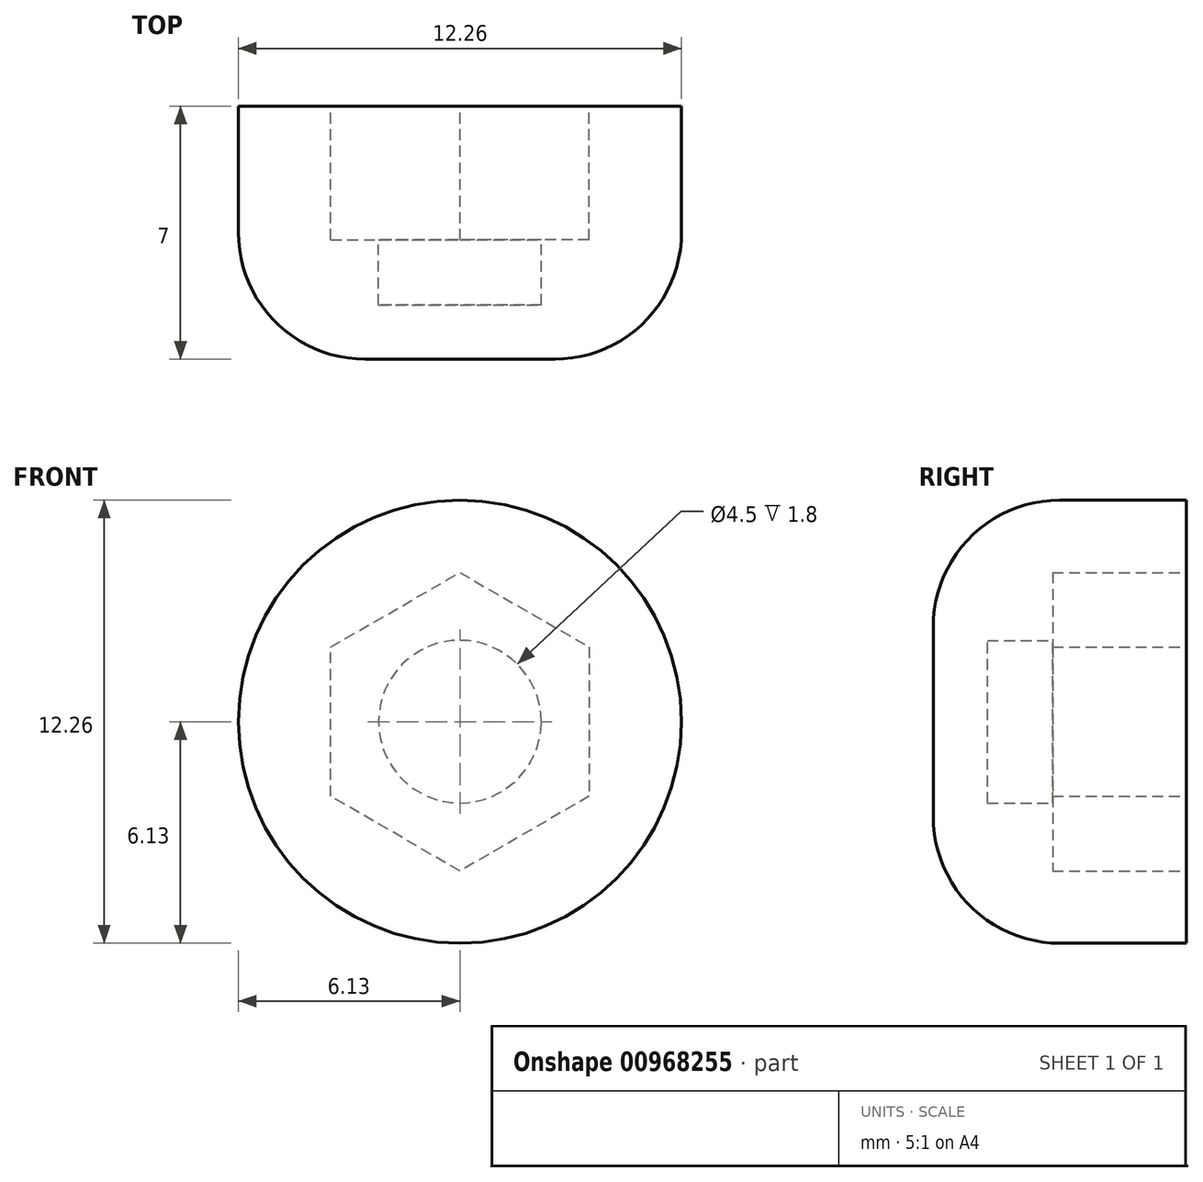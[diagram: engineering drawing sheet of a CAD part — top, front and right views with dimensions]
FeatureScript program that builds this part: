
annotation { "Feature Type Name" : "Feature", "Feature Type Description" : "" }
export const myFeature = defineFeature(function(context is Context, id is Id, definition is map)
    precondition{}
    {
        {
            var Q0;
            Q0=qCreatedBy(makeId("Front.planeOp"),FACE);
            var sketch = newSketch(context, id + "F0", { "sketchPlane" : qUnion([Q0])});
            skCircle(sketch, "E0", {"center": v(0, 0) * mm, "radius": 6.13 * mm});
            skCircle(sketch, "E1.cCircle", {"center": v(0, 0) * mm, "radius": 3.58 * mm, "construction": true});
            skLineSegment(sketch, "E1.0", {"start": v(3.57, -2.06) * mm, "end": v(0, -4.13) * mm});
            skLineSegment(sketch, "E1.1", {"start": v(0, -4.13) * mm, "end": v(-3.58, -2.06) * mm});
            skLineSegment(sketch, "E1.2", {"start": v(-3.58, -2.06) * mm, "end": v(-3.57, 2.06) * mm});
            skLineSegment(sketch, "E1.3", {"start": v(-3.58, 2.06) * mm, "end": v(0, 4.13) * mm});
            skLineSegment(sketch, "E1.4", {"start": v(0, 4.13) * mm, "end": v(3.57, 2.06) * mm});
            skLineSegment(sketch, "E1.5", {"start": v(3.58, 2.06) * mm, "end": v(3.57, -2.06) * mm});
            skPoint(sketch, "E1.0.midPoint", {"position": v(1.79, -3.1) * mm});
            skCircle(sketch, "E2", {"center": v(0, 0) * mm, "radius": 2.25 * mm});
            skSolve(sketch);
        }
        {
            var Q0;
            Q0=makeQuery(id+"F0.imprint","IMPRINT",FACE,{"disambiguationData":[TD([[makeQuery(id+"F0.imprint","IMPRINT",EDGE,{"derivedFrom":sQuery(id+"F0.wireOp",EDGE,"E0")}),1.0]])]});
            var Q1;
            Q1=makeQuery(id+"F0.imprint","IMPRINT",FACE,{"disambiguationData":[TD([[makeQuery(id+"F0.imprint","IMPRINT",EDGE,{"derivedFrom":sQuery(id+"F0.wireOp",EDGE,"E1.0")}),-1.0]])]});
            var Q2;
            Q2=makeQuery(id+"F0.imprint","IMPRINT",FACE,{"disambiguationData":[TD([[makeQuery(id+"F0.imprint","IMPRINT",EDGE,{"derivedFrom":sQuery(id+"F0.wireOp",EDGE,"E2")}),1.0]])]});
            extrude(context, id + "F1", {"entities" : qUnion([Q0, Q1, Q2]), "depth" : 7 * mm, "offsetDistance" : 25 * mm});
        }
        {
            var Q0;
            Q0=makeQuery(id+"F0.imprint","IMPRINT",FACE,{"disambiguationData":[TD([[makeQuery(id+"F0.imprint","IMPRINT",EDGE,{"derivedFrom":sQuery(id+"F0.wireOp",EDGE,"E2")}),1.0]])]});
            extrude(context, id + "F2", {"entities" : qUnion([Q0]), "operationType" : NewBodyOperationType.REMOVE, "depth" : (7 - 1.5) * mm, "offsetDistance" : 25 * mm});
        }
        {
            var Q0;
            Q0=makeQuery(id+"F0.imprint","IMPRINT",FACE,{"disambiguationData":[TD([[makeQuery(id+"F0.imprint","IMPRINT",EDGE,{"derivedFrom":sQuery(id+"F0.wireOp",EDGE,"E1.0")}),-1.0]])]});
            extrude(context, id + "F3", {"entities" : qUnion([Q0]), "operationType" : NewBodyOperationType.REMOVE, "depth" : (3.2 + 0.5) * mm, "offsetDistance" : 25 * mm});
        }
        {
            var Q0;
            Q0=makeQuery(id+"F1.opExtrude","CAP_EDGE",EDGE,{"disambiguationData":[OSD([sQuery(id+"F0.wireOp",EDGE,"E0")])],"isStart":false});
            fillet(context, id + "F4", {"entities" : qUnion([Q0]), "radius" : 3.5 * mm, "tangentPropagation" : true, "allowEdgeOverflow" : false});
        }
    });
